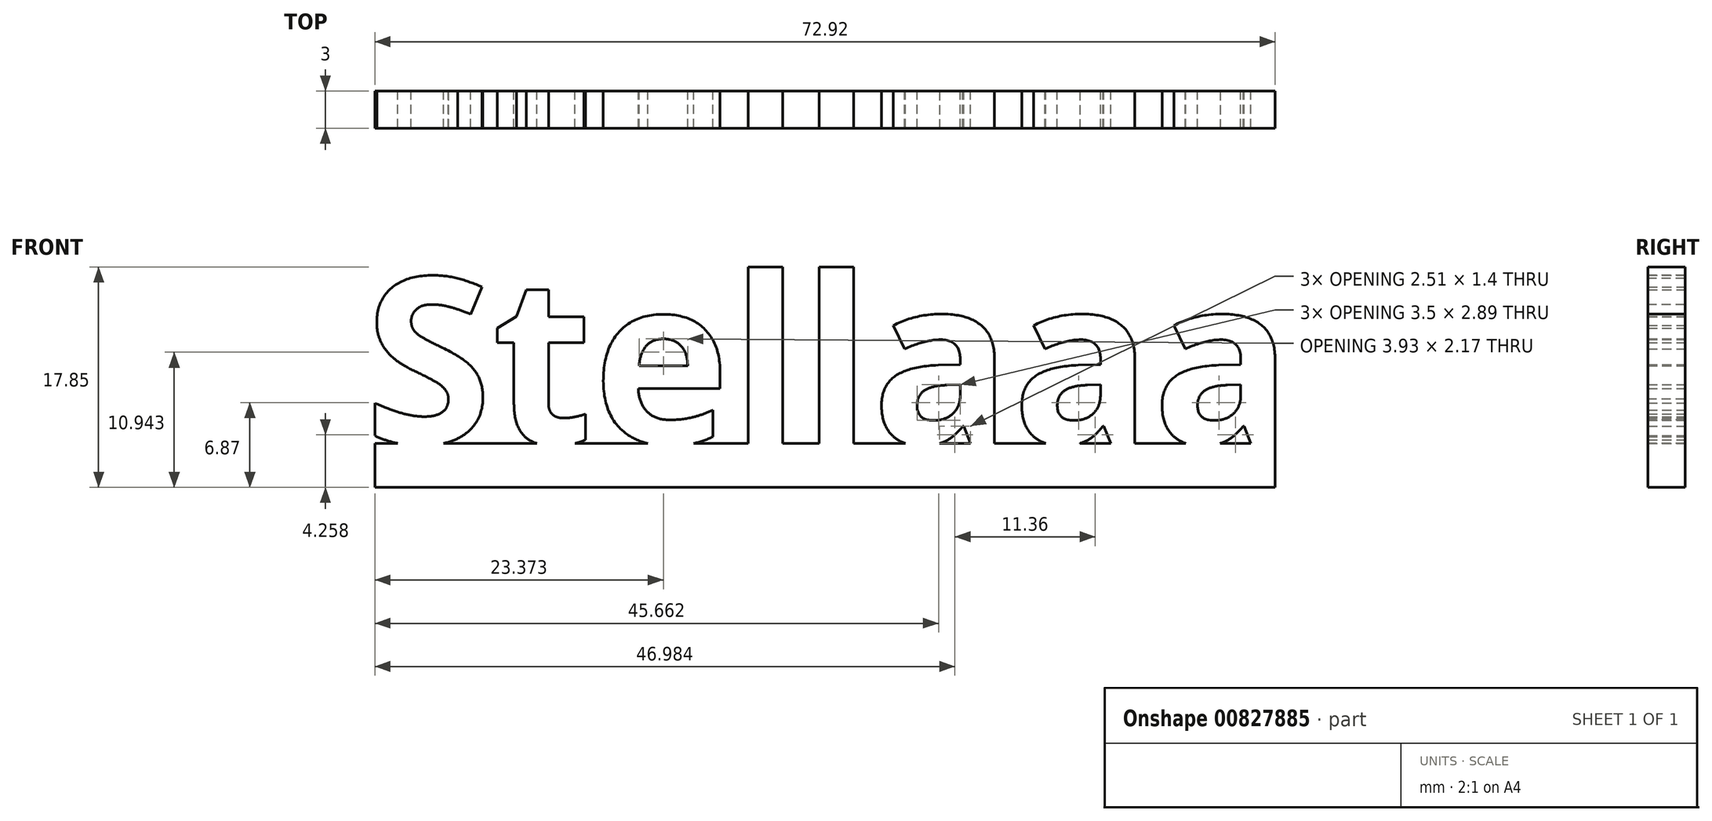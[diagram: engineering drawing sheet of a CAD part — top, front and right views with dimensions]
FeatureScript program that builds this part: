
annotation { "Feature Type Name" : "Feature", "Feature Type Description" : "" }
export const myFeature = defineFeature(function(context is Context, id is Id, definition is map)
    precondition{}
    {
        {
            var Q0;
            Q0=qCreatedBy(makeId("Front.planeOp"),FACE);
            var sketch = newSketch(context, id + "F0", { "sketchPlane" : qUnion([Q0])});
            skText(sketch, "E0", { "text": "Stellaaa", "fontName": "NotoSans-Bold.ttf"});
            const initialGuessF0  = {"E0": [-0.0375, 0, 1, 0, 0.01354]};
            skSetInitialGuess(sketch, initialGuessF0);
            skSolve(sketch);
        }
        {
            var Q0;
            Q0 = qSketchRegion(id + "F0", true);
            extrude(context, id + "F1", {"entities" : qUnion([Q0]), "depth" : 3 * mm, "offsetDistance" : 25 * mm});
        }
        {
            var Q0;
            Q0=makeQuery(id+"F1.opExtrude","CAP_FACE",FACE,{"disambiguationData":[OSD([sQuery(id+"F0.wireOp",EDGE,"E0.sketch_text.stroke-0"),sQuery(id+"F0.wireOp",EDGE,"E0.sketch_text.stroke-1"),sQuery(id+"F0.wireOp",EDGE,"E0.sketch_text.stroke-2"),sQuery(id+"F0.wireOp",EDGE,"E0.sketch_text.stroke-3"),sQuery(id+"F0.wireOp",EDGE,"E0.sketch_text.stroke-4"),sQuery(id+"F0.wireOp",EDGE,"E0.sketch_text.stroke-5"),sQuery(id+"F0.wireOp",EDGE,"E0.sketch_text.stroke-6"),sQuery(id+"F0.wireOp",EDGE,"E0.sketch_text.stroke-7"),sQuery(id+"F0.wireOp",EDGE,"E0.sketch_text.stroke-8"),sQuery(id+"F0.wireOp",EDGE,"E0.sketch_text.stroke-9"),sQuery(id+"F0.wireOp",EDGE,"E0.sketch_text.stroke-10"),sQuery(id+"F0.wireOp",EDGE,"E0.sketch_text.stroke-11"),sQuery(id+"F0.wireOp",EDGE,"E0.sketch_text.stroke-12"),sQuery(id+"F0.wireOp",EDGE,"E0.sketch_text.stroke-13"),sQuery(id+"F0.wireOp",EDGE,"E0.sketch_text.stroke-14"),sQuery(id+"F0.wireOp",EDGE,"E0.sketch_text.stroke-15"),sQuery(id+"F0.wireOp",EDGE,"E0.sketch_text.stroke-16"),sQuery(id+"F0.wireOp",EDGE,"E0.sketch_text.stroke-17"),sQuery(id+"F0.wireOp",EDGE,"E0.sketch_text.stroke-18"),sQuery(id+"F0.wireOp",EDGE,"E0.sketch_text.stroke-19"),sQuery(id+"F0.wireOp",EDGE,"E0.sketch_text.stroke-20"),sQuery(id+"F0.wireOp",EDGE,"E0.sketch_text.stroke-21"),sQuery(id+"F0.wireOp",EDGE,"E0.sketch_text.stroke-22"),sQuery(id+"F0.wireOp",EDGE,"E0.sketch_text.stroke-23"),sQuery(id+"F0.wireOp",EDGE,"E0.sketch_text.stroke-24"),sQuery(id+"F0.wireOp",EDGE,"E0.sketch_text.stroke-25"),sQuery(id+"F0.wireOp",EDGE,"E0.sketch_text.stroke-26"),sQuery(id+"F0.wireOp",EDGE,"E0.sketch_text.stroke-27")])],"isStart":false});
            var sketch = newSketch(context, id + "F2", { "sketchPlane" : qUnion([Q0])});
            skLineSegment(sketch, "E1.bottom", {"start": v(-36.64, 0) * mm, "end": v(36.28, 0) * mm});
            skLineSegment(sketch, "E1.top", {"start": v(-36.64, -3.56) * mm, "end": v(36.28, -3.56) * mm});
            skLineSegment(sketch, "E1.left", {"start": v(-36.64, 0) * mm, "end": v(-36.64, -3.56) * mm});
            skLineSegment(sketch, "E1.right", {"start": v(36.28, 0) * mm, "end": v(36.28, -3.56) * mm});
            skSolve(sketch);
        }
        {
            var Q0;
            Q0 = qSketchRegion(id + "F2", true);
            extrude(context, id + "F3", {"entities" : qUnion([Q0]), "operationType" : NewBodyOperationType.ADD, "oppositeDirection" : true, "depth" : 3 * mm, "offsetDistance" : 25 * mm});
        }
    });
